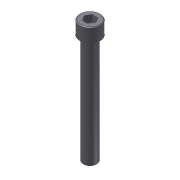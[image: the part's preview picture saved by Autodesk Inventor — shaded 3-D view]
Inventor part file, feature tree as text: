
AUTODESK INVENTOR PART (.ipt)
format: ipt  version: 2012 (Build 160160000, 160)  size: 102,912 bytes
history: native  units: in
note: dims shown in document units (in); Inventor stores cm internally (conversion verified against a paired STEP export)
features: extrude x3, sketch x3, fillet x1
ambient origin geometry x8: Origin, YZ Plane, XZ Plane, XY Plane, X Axis, Y Axis, Z Axis, Center Point
bodies: Solid1 (feature_tree)
feature tree (7):
  extrude  "Extrusion1"  Depth=2.0in TaperAngle=0.0deg
  extrude  "Extrusion2"  Depth=0.25in TaperAngle=0.0deg
  extrude  "Extrusion3"  Depth=0.125in TaperAngle=0.0deg
  fillet  "Fillet1"  Radius=0.0156in
  sketch  "Sketch1"  dims[d0=0.25in d1=2.0in d2=0.0in]
  sketch  "Sketch2"  dims[d3=0.375in d4=0.25in d5=0.0in]
  sketch  "Sketch3"  dims[d6=0.1875in d7=0.125in d8=0.0in d9=0.0156in]
